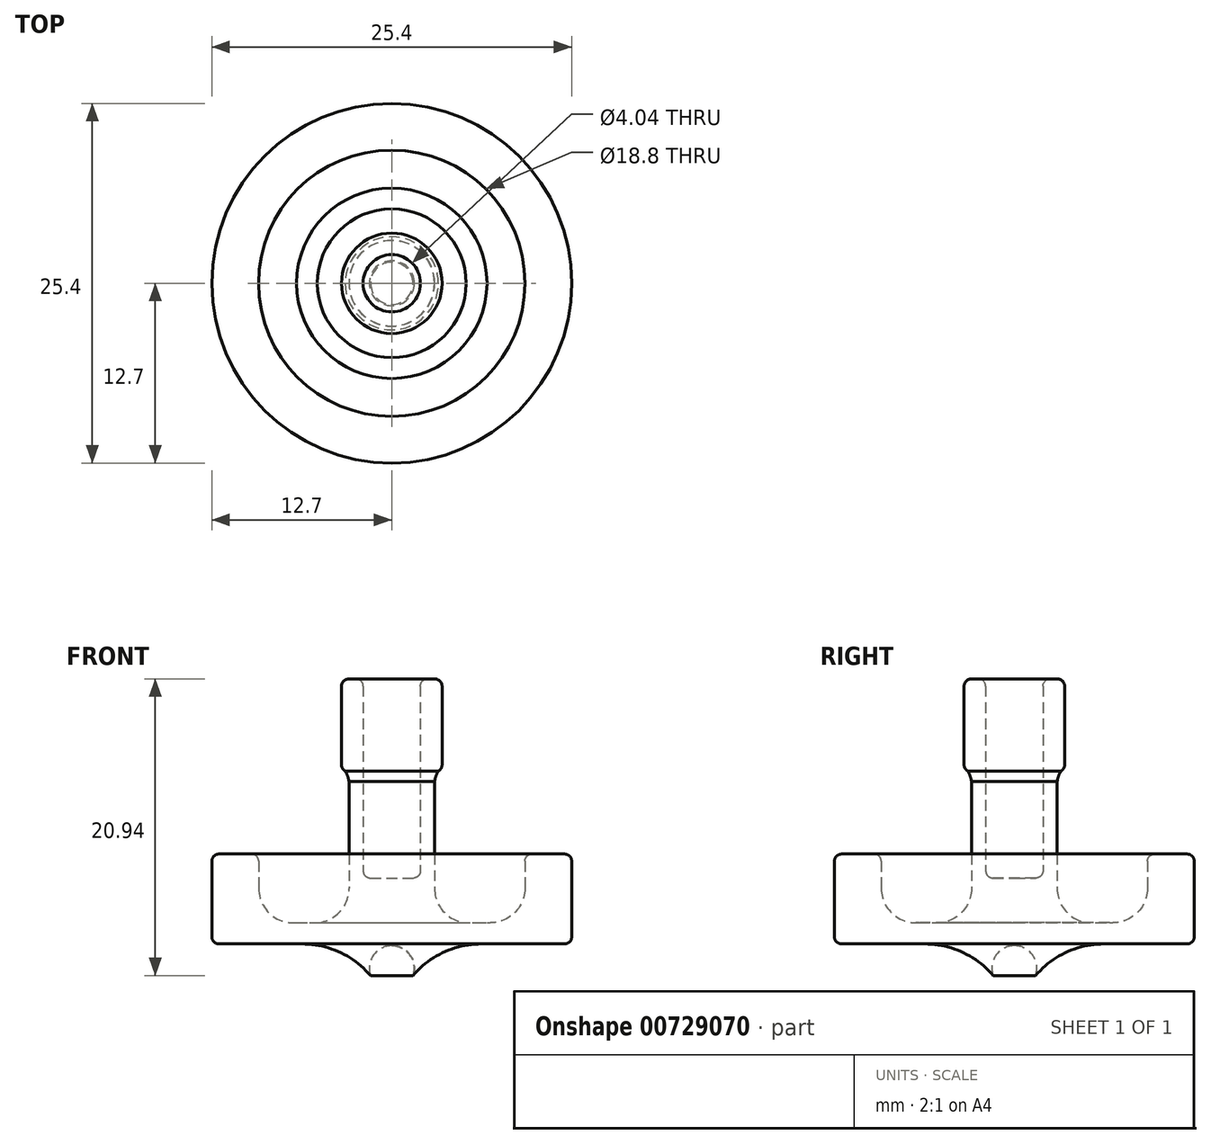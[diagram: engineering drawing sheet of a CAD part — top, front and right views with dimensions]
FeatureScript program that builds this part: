
annotation { "Feature Type Name" : "Feature", "Feature Type Description" : "" }
export const myFeature = defineFeature(function(context is Context, id is Id, definition is map)
    precondition{}
    {
        {
            var Q0;
            Q0=qCreatedBy(makeId("Front.planeOp"),FACE);
            var sketch = newSketch(context, id + "F0", { "sketchPlane" : qUnion([Q0])});
            skLineSegment(sketch, "E0.bottom", {"start": v(-6.35, 0) * mm, "end": v(-12.2, 0) * mm});
            skLineSegment(sketch, "E0.left", {"start": v(0, 0) * mm, "end": v(0, 6.35) * mm});
            skLineSegment(sketch, "E0.right", {"start": v(-12.7, 0.5) * mm, "end": v(-12.7, 5.85) * mm});
            skLineSegment(sketch, "E1", {"start": v(-9.4, 5.85) * mm, "end": v(-9.4, 3.93) * mm});
            skPoint(sketch, "E2.orphan", {"position": v(-12.7, 1.5) * mm});
            skPoint(sketch, "E3.end.orphan", {"position": v(-6.35, 0) * mm});
            skPoint(sketch, "E3.start.orphan", {"position": v(-6.35, 1.5) * mm});
            skLineSegment(sketch, "E4.trimOffspring", {"start": v(-9.9, 6.35) * mm, "end": v(-12.2, 6.35) * mm});
            skPoint(sketch, "E5.orphan", {"position": v(0, 1.5) * mm});
            skArc(sketch, "E6", {"start": v(-9.4, 3.93) * mm, "mid": v(-8.6, 2.13) * mm, "end": v(-6.72, 1.5) * mm});
            skPoint(sketch, "E7.orphan", {"position": v(-4.05, 1.5) * mm});
            skPoint(sketch, "E8.orphan", {"position": v(-9.4, 1.5) * mm});
            skLineSegment(sketch, "E9.top", {"start": v(0, 4.66) * mm, "end": v(-1.52, 4.66) * mm});
            skLineSegment(sketch, "E9.left", {"start": v(0, 6.35) * mm, "end": v(0, 4.66) * mm});
            skLineSegment(sketch, "E9.right", {"start": v(-2.02, 18.71) * mm, "end": v(-2.02, 5.16) * mm});
            skPoint(sketch, "E10.visualSharp", {"position": v(-12.7, 0) * mm});
            skArc(sketch, "E10.filletArc", {"start": v(-12.7, 0.5) * mm, "mid": v(-12.55, 0.15) * mm, "end": v(-12.2, 0) * mm});
            skPoint(sketch, "E11.visualSharp", {"position": v(-4.05, 20) * mm});
            skPoint(sketch, "E12.visualSharp", {"position": v(-12.7, 6.35) * mm});
            skArc(sketch, "E12.filletArc", {"start": v(-12.2, 6.35) * mm, "mid": v(-12.55, 6.2) * mm, "end": v(-12.7, 5.85) * mm});
            skPoint(sketch, "E13.visualSharp", {"position": v(-9.4, 6.35) * mm});
            skArc(sketch, "E13.filletArc", {"start": v(-9.4, 5.85) * mm, "mid": v(-9.55, 6.2) * mm, "end": v(-9.9, 6.35) * mm});
            skPoint(sketch, "E14.visualSharp", {"position": v(-2.02, 4.66) * mm});
            skArc(sketch, "E14.filletArc", {"start": v(-2.02, 5.16) * mm, "mid": v(-1.87, 4.8) * mm, "end": v(-1.52, 4.66) * mm});
            skArc(sketch, "E15", {"start": v(0, -0.12) * mm, "mid": v(-1.3, -0.8) * mm, "end": v(-1.5, -2.23) * mm});
            skLineSegment(sketch, "E16", {"start": v(0, 0) * mm, "end": v(0, -0.12) * mm});
            skArc(sketch, "E17", {"start": v(-1.5, -2.23) * mm, "mid": v(-3.68, -0.58) * mm, "end": v(-6.35, 0) * mm});
            skLineSegment(sketch, "E18.right", {"start": v(-4.5, 19.53) * mm, "end": v(-4.5, 19.51) * mm});
            skPoint(sketch, "E19.start.orphan", {"position": v(-4.05, 13.45) * mm});
            skArc(sketch, "E20", {"start": v(-4.5, 19.53) * mm, "mid": v(-4.5, 19.52) * mm, "end": v(-4.5, 19.51) * mm});
            skPoint(sketch, "E21.end.orphan", {"position": v(-4.05, 3.93) * mm});
            skPoint(sketch, "E22.end.orphan", {"position": v(-4.05, 6.35) * mm});
            skPoint(sketch, "E23.end.orphan", {"position": v(-4.5, 13.45) * mm});
            skLineSegment(sketch, "E24", {"start": v(-3.02, 9.9) * mm, "end": v(-3.02, 3.93) * mm});
            skLineSegment(sketch, "E25", {"start": v(-2.02, 18.71) * mm, "end": v(-3.03, 18.71) * mm});
            skArc(sketch, "E26", {"start": v(-5.25, 1.5) * mm, "mid": v(-3.66, 2.28) * mm, "end": v(-3.02, 3.93) * mm});
            skLineSegment(sketch, "E27", {"start": v(-6.72, 1.5) * mm, "end": v(-5.25, 1.5) * mm});
            skLineSegment(sketch, "E28.bottom", {"start": v(-3.03, 18.71) * mm, "end": v(-3.55, 18.71) * mm});
            skLineSegment(sketch, "E28.top", {"start": v(-3.29, 12.21) * mm, "end": v(-3.55, 12.21) * mm});
            skLineSegment(sketch, "E28.right", {"start": v(-3.55, 18.71) * mm, "end": v(-3.55, 12.21) * mm});
            skLineSegment(sketch, "E29", {"start": v(-3.02, 11.49) * mm, "end": v(-3.02, 9.9) * mm});
            skArc(sketch, "E30", {"start": v(-3.02, 11.49) * mm, "mid": v(-3.13, 11.86) * mm, "end": v(-3.29, 12.21) * mm});
            skPoint(sketch, "E31.orphan", {"position": v(-3.03, 12.21) * mm});
            skSolve(sketch);
        }
        {
            var Q0;
            Q0=makeQuery(id+"F0.imprint","IMPRINT",FACE,{"disambiguationData":[TD([[makeQuery(id+"F0.imprint","IMPRINT",EDGE,{"derivedFrom":sQuery(id+"F0.wireOp",EDGE,"E0.bottom")}),-1.0]])]});
            var Q1;
            {var subQ1=sQuery(id+"F0.wireOp",EDGE,"ff6280aa-fd3c-4f03-93f3-c40663dc82ce.top");Q1=makeQuery(id+"F0.imprint","IMPRINT",FACE,{"disambiguationData":[TD([[makeQuery(id+"F0.imprint","IMPRINT",EDGE,{"derivedFrom":subQ1}),1.0]])]});}
            var Q2;
            Q2=sQuery(id+"F0.wireOp",EDGE,"E0.left");
            revolve(context, id + "F1", {"surfaceOperationType" : NewSurfaceOperationType.NEW, "entities" : qUnion([Q0, Q1]), "axis" : qUnion([Q2]), "revolveType" : RevolveType.FULL});
        }
        {
            var Q0;
            Q0=makeQuery(id+"F1.opRevolve","SWEPT_EDGE",EDGE,{"disambiguationData":[OSD([sQuery(id+"F0.wireOp",EDGE,"E28.bottom"),sQuery(id+"F0.wireOp",EDGE,"E28.right")])]});
            var Q1;
            Q1=makeQuery(id+"F1.opRevolve","SWEPT_EDGE",EDGE,{"disambiguationData":[OSD([sQuery(id+"F0.wireOp",EDGE,"E28.top"),sQuery(id+"F0.wireOp",EDGE,"E28.right")])]});
            fillet(context, id + "F2", {"entities" : qUnion([Q0, Q1]), "radius" : .5 * mm, "tangentPropagation" : true, "allowEdgeOverflow" : false});
        }
        {
            var Q0;
            Q0=makeQuery(id+"F1.opRevolve","SWEPT_EDGE",EDGE,{"disambiguationData":[OSD([sQuery(id+"F0.wireOp",EDGE,"E9.right"),sQuery(id+"F0.wireOp",EDGE,"E25")])]});
            fillet(context, id + "F3", {"entities" : qUnion([Q0]), "radius" : .5 * mm, "tangentPropagation" : true, "allowEdgeOverflow" : false});
        }
    });
